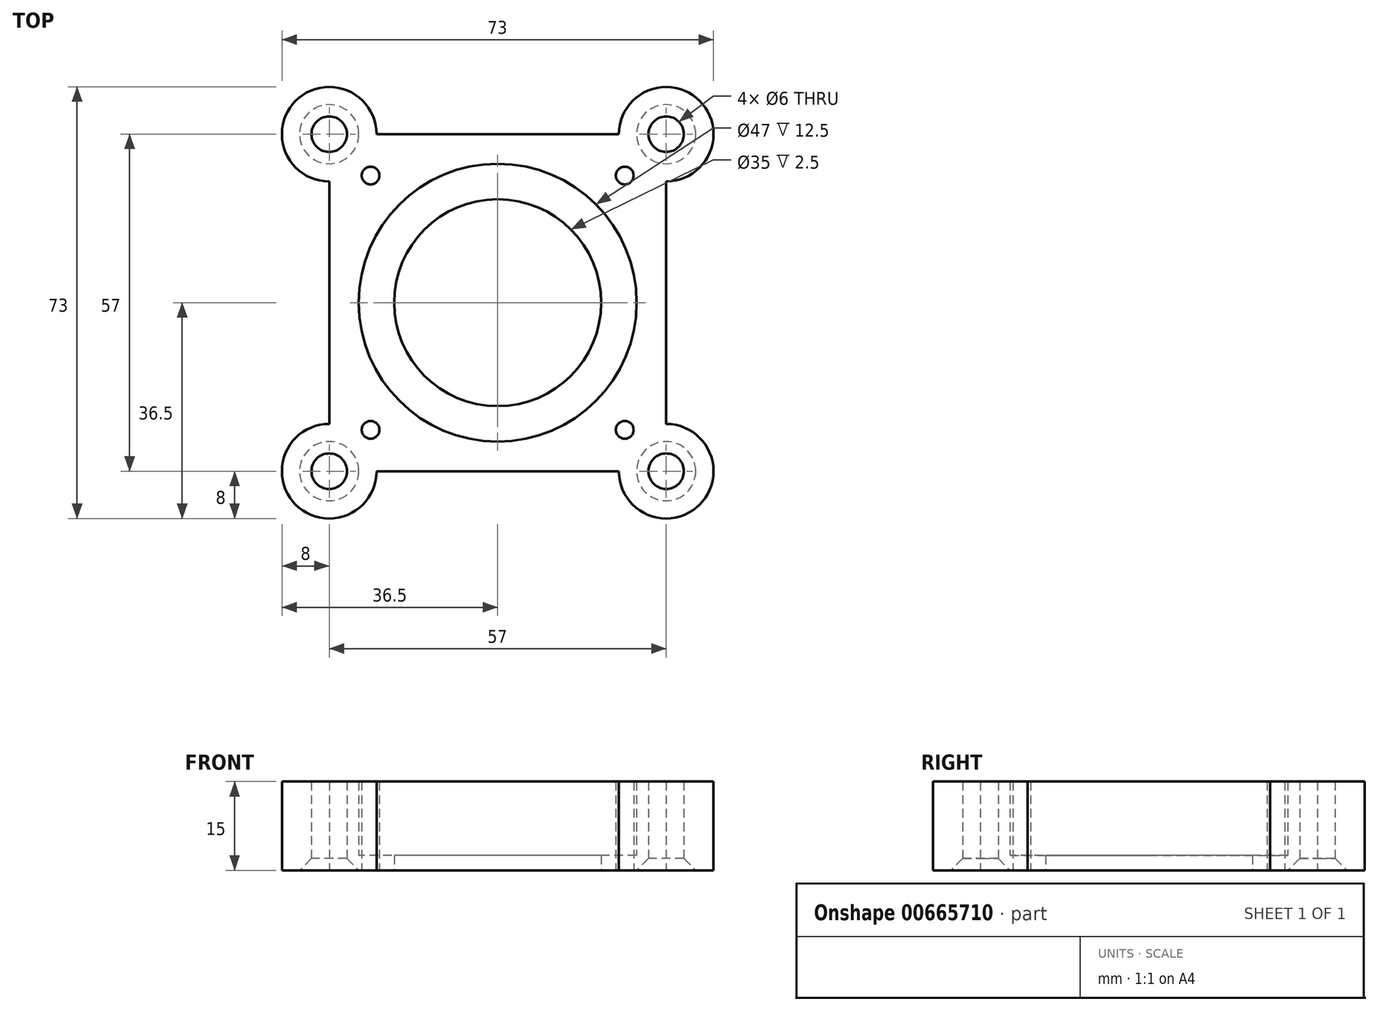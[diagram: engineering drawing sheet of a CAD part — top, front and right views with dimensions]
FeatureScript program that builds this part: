
annotation { "Feature Type Name" : "Feature", "Feature Type Description" : "" }
export const myFeature = defineFeature(function(context is Context, id is Id, definition is map)
    precondition{}
    {
        {
            var Q0;
            Q0=qCreatedBy(makeId("Top.planeOp"),FACE);
            var sketch = newSketch(context, id + "F0", { "sketchPlane" : qUnion([Q0])});
            skCircle(sketch, "E0", {"center": v(0, 0) * mm, "radius": 12.5 * mm});
            skCircle(sketch, "E1", {"center": v(0, 0) * mm, "radius": 23.5 * mm});
            skLineSegment(sketch, "E2.bottom", {"start": v(36.5, -36.5) * mm, "end": v(-36.5, -36.5) * mm});
            skLineSegment(sketch, "E2.top", {"start": v(36.5, 36.5) * mm, "end": v(-36.5, 36.5) * mm});
            skLineSegment(sketch, "E2.left", {"start": v(36.5, -36.5) * mm, "end": v(36.5, 36.5) * mm});
            skLineSegment(sketch, "E2.right", {"start": v(-36.5, -36.5) * mm, "end": v(-36.5, 36.5) * mm});
            skLineSegment(sketch, "E3.bottom", {"start": v(28.5, -28.5) * mm, "end": v(-28.5, -28.5) * mm});
            skLineSegment(sketch, "E3.top", {"start": v(28.5, 28.5) * mm, "end": v(-28.5, 28.5) * mm});
            skLineSegment(sketch, "E3.left", {"start": v(28.5, -28.5) * mm, "end": v(28.5, 28.5) * mm});
            skLineSegment(sketch, "E3.right", {"start": v(-28.5, -28.5) * mm, "end": v(-28.5, 28.5) * mm});
            skCircle(sketch, "E4", {"center": v(-28.5, 28.5) * mm, "radius": 3 * mm});
            skCircle(sketch, "E5", {"center": v(28.5, 28.5) * mm, "radius": 3 * mm});
            skCircle(sketch, "E6", {"center": v(28.5, -28.5) * mm, "radius": 3 * mm});
            skCircle(sketch, "E7", {"center": v(-28.5, -28.5) * mm, "radius": 3 * mm});
            skCircle(sketch, "E8", {"center": v(0, 0) * mm, "radius": 17.5 * mm});
            skCircle(sketch, "E9", {"center": v(0, 0) * mm, "radius": 15 * mm});
            skCircle(sketch, "E10", {"center": v(-28.5, 28.5) * mm, "radius": 8 * mm});
            skCircle(sketch, "E11", {"center": v(28.5, 28.5) * mm, "radius": 8 * mm});
            skCircle(sketch, "E12", {"center": v(28.5, -28.5) * mm, "radius": 8 * mm});
            skCircle(sketch, "E13", {"center": v(-28.5, -28.5) * mm, "radius": 8 * mm});
            skLineSegment(sketch, "E14.bottom", {"start": v(-21.5, 21.5) * mm, "end": v(21.5, 21.5) * mm, "construction": true});
            skLineSegment(sketch, "E14.top", {"start": v(-21.5, -21.5) * mm, "end": v(21.5, -21.5) * mm, "construction": true});
            skLineSegment(sketch, "E14.left", {"start": v(-21.5, 21.5) * mm, "end": v(-21.5, -21.5) * mm, "construction": true});
            skLineSegment(sketch, "E14.right", {"start": v(21.5, 21.5) * mm, "end": v(21.5, -21.5) * mm, "construction": true});
            skCircle(sketch, "E15", {"center": v(-21.5, 21.5) * mm, "radius": 1.5 * mm});
            skCircle(sketch, "E16", {"center": v(21.5, 21.5) * mm, "radius": 1.5 * mm});
            skCircle(sketch, "E17", {"center": v(21.5, -21.5) * mm, "radius": 1.5 * mm});
            skCircle(sketch, "E18", {"center": v(-21.5, -21.5) * mm, "radius": 1.5 * mm});
            skSolve(sketch);
        }
        {
            var Q0;
            {var subQ0=sQuery(id+"F0.wireOp",EDGE,"E10");var subQ1=sQuery(id+"F0.wireOp",EDGE,"E3.top");var subQ2=makeQuery(id+"F0.imprint","INTERSECT",VERTEX,{"derivedFrom":[subQ1,subQ0]});Q0=makeQuery(id+"F0.imprint","IMPRINT",FACE,{"disambiguationData":[TD([[makeQuery(id+"F0.imprint","IMPRINT",EDGE,{"disambiguationData":[TD([[subQ2,-1.0]])],"derivedFrom":subQ1}),1.0]])]});}
            var Q1;
            Q1=makeQuery(id+"F0.imprint","IMPRINT",FACE,{"disambiguationData":[TD([[makeQuery(id+"F0.imprint","IMPRINT",EDGE,{"derivedFrom":sQuery(id+"F0.wireOp",EDGE,"E1")}),-1.0]])]});
            var Q2;
            {var subQ0=sQuery(id+"F0.wireOp",EDGE,"E5");var subQ1=sQuery(id+"F0.wireOp",EDGE,"E3.top");var subQ2=makeQuery(id+"F0.imprint","INTERSECT",VERTEX,{"derivedFrom":[subQ1,subQ0]});Q2=makeQuery(id+"F0.imprint","IMPRINT",FACE,{"disambiguationData":[TD([[makeQuery(id+"F0.imprint","IMPRINT",EDGE,{"disambiguationData":[TD([[subQ2,-1.0]])],"derivedFrom":subQ1}),1.0]])]});}
            var Q3;
            {var subQ3=sQuery(id+"F0.wireOp",EDGE,"E5");var subQ4=sQuery(id+"F0.wireOp",EDGE,"E3.top");var subQ5=makeQuery(id+"F0.imprint","INTERSECT",VERTEX,{"derivedFrom":[subQ4,subQ3]});Q3=makeQuery(id+"F0.imprint","IMPRINT",FACE,{"disambiguationData":[TD([[makeQuery(id+"F0.imprint","IMPRINT",EDGE,{"disambiguationData":[TD([[subQ5,-1.0]])],"derivedFrom":subQ4}),-1.0]])]});}
            var Q4;
            {var subQ4=sQuery(id+"F0.wireOp",EDGE,"E6");var subQ5=sQuery(id+"F0.wireOp",EDGE,"E3.bottom");var subQ6=makeQuery(id+"F0.imprint","INTERSECT",VERTEX,{"derivedFrom":[subQ5,subQ4]});Q4=makeQuery(id+"F0.imprint","IMPRINT",FACE,{"disambiguationData":[TD([[makeQuery(id+"F0.imprint","IMPRINT",EDGE,{"disambiguationData":[TD([[subQ6,-1.0]])],"derivedFrom":subQ5}),1.0]])]});}
            var Q5;
            {var subQ0=sQuery(id+"F0.wireOp",EDGE,"E6");var subQ1=sQuery(id+"F0.wireOp",EDGE,"E3.bottom");var subQ2=makeQuery(id+"F0.imprint","INTERSECT",VERTEX,{"derivedFrom":[subQ1,subQ0]});Q5=makeQuery(id+"F0.imprint","IMPRINT",FACE,{"disambiguationData":[TD([[makeQuery(id+"F0.imprint","IMPRINT",EDGE,{"disambiguationData":[TD([[subQ2,-1.0]])],"derivedFrom":subQ1}),-1.0]])]});}
            var Q6;
            {var subQ0=sQuery(id+"F0.wireOp",EDGE,"E13");var subQ1=sQuery(id+"F0.wireOp",EDGE,"E3.bottom");var subQ2=makeQuery(id+"F0.imprint","INTERSECT",VERTEX,{"derivedFrom":[subQ1,subQ0]});Q6=makeQuery(id+"F0.imprint","IMPRINT",FACE,{"disambiguationData":[TD([[makeQuery(id+"F0.imprint","IMPRINT",EDGE,{"disambiguationData":[TD([[subQ2,-1.0]])],"derivedFrom":subQ1}),-1.0]])]});}
            var Q7;
            {var subQ1=sQuery(id+"F0.wireOp",EDGE,"E3.bottom");var subQ5=sQuery(id+"F0.wireOp",EDGE,"E13");var subQ8=makeQuery(id+"F0.imprint","INTERSECT",VERTEX,{"derivedFrom":[subQ1,subQ5]});Q7=makeQuery(id+"F0.imprint","IMPRINT",FACE,{"disambiguationData":[TD([[makeQuery(id+"F0.imprint","IMPRINT",EDGE,{"disambiguationData":[TD([[subQ8,-1.0]])],"derivedFrom":subQ1}),1.0]])]});}
            var Q8;
            {var subQ0=sQuery(id+"F0.wireOp",EDGE,"E18");var subQ1=sQuery(id+"F0.wireOp",EDGE,"E13");var subQ2=makeQuery(id+"F0.imprint","INTERSECT",VERTEX,{"disambiguationData":[OD(0.0)],"derivedFrom":[subQ1,subQ0]});Q8=makeQuery(id+"F0.imprint","IMPRINT",FACE,{"disambiguationData":[TD([[makeQuery(id+"F0.imprint","IMPRINT",EDGE,{"disambiguationData":[TD([[subQ2,-1.0]])],"derivedFrom":subQ1}),1.0]])]});}
            var Q9;
            {var subQ0=sQuery(id+"F0.wireOp",EDGE,"E17");var subQ1=sQuery(id+"F0.wireOp",EDGE,"E12");var subQ2=makeQuery(id+"F0.imprint","INTERSECT",VERTEX,{"disambiguationData":[OD(0.0)],"derivedFrom":[subQ1,subQ0]});Q9=makeQuery(id+"F0.imprint","IMPRINT",FACE,{"disambiguationData":[TD([[makeQuery(id+"F0.imprint","IMPRINT",EDGE,{"disambiguationData":[TD([[subQ2,-1.0]])],"derivedFrom":subQ1}),1.0]])]});}
            var Q10;
            {var subQ0=sQuery(id+"F0.wireOp",EDGE,"E16");var subQ1=sQuery(id+"F0.wireOp",EDGE,"E11");var subQ2=makeQuery(id+"F0.imprint","INTERSECT",VERTEX,{"disambiguationData":[OD(0.0)],"derivedFrom":[subQ1,subQ0]});Q10=makeQuery(id+"F0.imprint","IMPRINT",FACE,{"disambiguationData":[TD([[makeQuery(id+"F0.imprint","IMPRINT",EDGE,{"disambiguationData":[TD([[subQ2,-1.0]])],"derivedFrom":subQ1}),1.0]])]});}
            var Q11;
            {var subQ0=sQuery(id+"F0.wireOp",EDGE,"E10");var subQ2=sQuery(id+"F0.wireOp",EDGE,"E3.top");var subQ3=makeQuery(id+"F0.imprint","INTERSECT",VERTEX,{"derivedFrom":[subQ2,subQ0]});Q11=makeQuery(id+"F0.imprint","IMPRINT",FACE,{"disambiguationData":[TD([[makeQuery(id+"F0.imprint","IMPRINT",EDGE,{"disambiguationData":[TD([[subQ3,-1.0]])],"derivedFrom":subQ2}),-1.0]])]});}
            extrude(context, id + "F1", {"entities" : qUnion([Q0, Q1, Q2, Q3, Q4, Q5, Q6, Q7, Q8, Q9, Q10, Q11]), "depth" : 15 * mm, "offsetDistance" : 25 * mm});
        }
        {
            var Q0;
            Q0=makeQuery(id+"F0.imprint","IMPRINT",FACE,{"disambiguationData":[TD([[makeQuery(id+"F0.imprint","IMPRINT",EDGE,{"derivedFrom":sQuery(id+"F0.wireOp",EDGE,"E1")}),1.0]])]});
            extrude(context, id + "F2", {"entities" : qUnion([Q0]), "operationType" : NewBodyOperationType.ADD, "depth" : 2.5 * mm, "offsetDistance" : 25 * mm});
        }
        {
            var Q0;
            Q0=makeQuery(id+"F1.opExtrude","CAP_EDGE",EDGE,{"disambiguationData":[OSD([sQuery(id+"F0.wireOp",EDGE,"E5")])],"isStart":true});
            var Q1;
            Q1=makeQuery(id+"F1.opExtrude","CAP_EDGE",EDGE,{"disambiguationData":[OSD([sQuery(id+"F0.wireOp",EDGE,"E4")])],"isStart":true});
            var Q2;
            Q2=makeQuery(id+"F1.opExtrude","CAP_EDGE",EDGE,{"disambiguationData":[OSD([sQuery(id+"F0.wireOp",EDGE,"E7")])],"isStart":true});
            var Q3;
            Q3=makeQuery(id+"F1.opExtrude","CAP_EDGE",EDGE,{"disambiguationData":[OSD([sQuery(id+"F0.wireOp",EDGE,"E6")])],"isStart":true});
            chamfer(context, id + "F3", {"entities" : qUnion([Q0, Q1, Q2, Q3]), "width" : 2 * mm, "tangentPropagation" : true});
        }
    });
